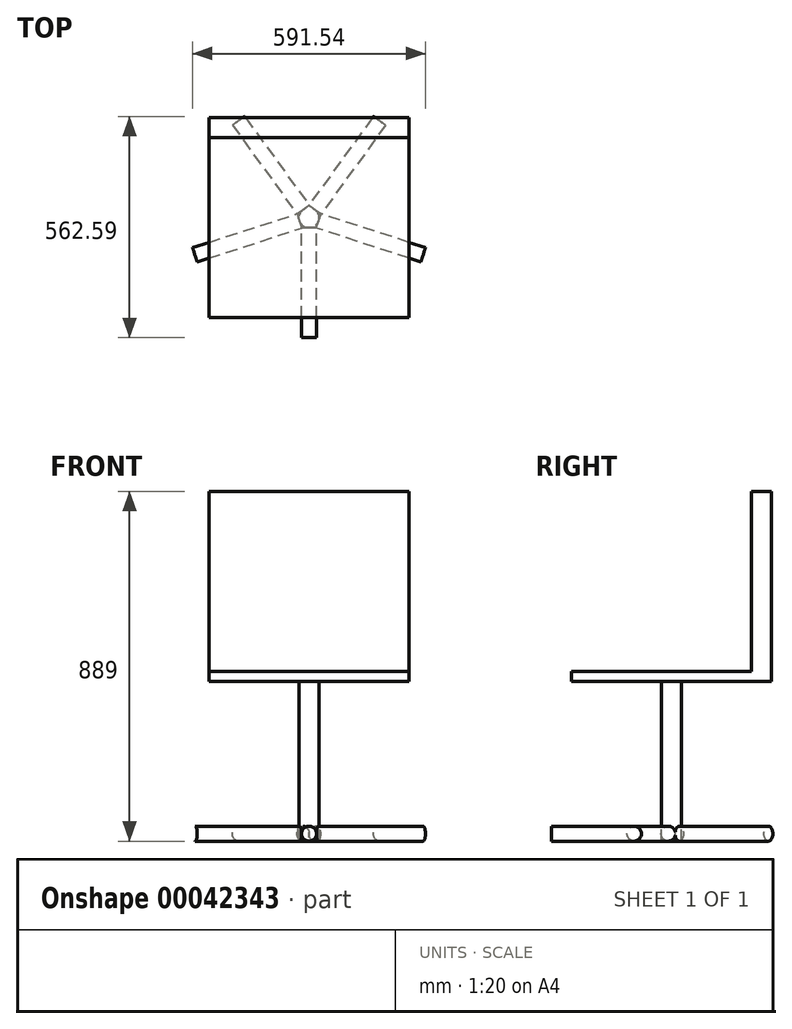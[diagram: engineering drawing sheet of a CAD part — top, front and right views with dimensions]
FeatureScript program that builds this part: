
annotation { "Feature Type Name" : "Feature", "Feature Type Description" : "" }
export const myFeature = defineFeature(function(context is Context, id is Id, definition is map)
    precondition{}
    {
        {
            var Q0;
            Q0=qCreatedBy(makeId("Top.planeOp"),FACE);
            var sketch = newSketch(context, id + "F0", { "sketchPlane" : qUnion([Q0])});
            skLineSegment(sketch, "E0.rect.bottom", {"start": v(254, 254) * mm, "end": v(-254, 254) * mm});
            skLineSegment(sketch, "E0.rect.top", {"start": v(254, -254) * mm, "end": v(-254, -254) * mm});
            skLineSegment(sketch, "E0.rect.left", {"start": v(254, 254) * mm, "end": v(254, -254) * mm});
            skLineSegment(sketch, "E0.rect.right", {"start": v(-254, 254) * mm, "end": v(-254, -254) * mm});
            skPoint(sketch, "E0.rect.middle", {"position": v(0, 0) * mm});
            skSolve(sketch);
        }
        {
            var Q0;
            Q0=qSketchRegion(id+"F0",true);
            extrude(context, id + "F1", {"entities" : qUnion([Q0]), "oppositeDirection" : true, "depth" : 25.4 * mm});
        }
        {
            var Q0;
            Q0=makeQuery(id+"F1.opExtrude","CAP_FACE",FACE,{"disambiguationData":[OSD([sQuery(id+"F0.wireOp",EDGE,"E0.rect.bottom"),sQuery(id+"F0.wireOp",EDGE,"E0.rect.top"),sQuery(id+"F0.wireOp",EDGE,"E0.rect.left"),sQuery(id+"F0.wireOp",EDGE,"E0.rect.right")])],"isStart":true});
            var sketch = newSketch(context, id + "F2", { "sketchPlane" : qUnion([Q0])});
            skLineSegment(sketch, "E1.bottom", {"start": v(-254, 254) * mm, "end": v(254, 254) * mm});
            skLineSegment(sketch, "E1.top", {"start": v(-254, 203.2) * mm, "end": v(254, 203.2) * mm});
            skLineSegment(sketch, "E1.left", {"start": v(-254, 254) * mm, "end": v(-254, 203.2) * mm});
            skLineSegment(sketch, "E1.right", {"start": v(254, 254) * mm, "end": v(254, 203.2) * mm});
            skSolve(sketch);
        }
        {
            var Q0;
            Q0=qSketchRegion(id+"F2",true);
            extrude(context, id + "F3", {"entities" : qUnion([Q0]), "operationType" : NewBodyOperationType.ADD, "depth" : 457.2 * mm});
        }
        {
            var Q0;
            Q0=makeQuery(id+"F1.opExtrude","CAP_FACE",FACE,{"disambiguationData":[OSD([sQuery(id+"F0.wireOp",EDGE,"E0.rect.bottom"),sQuery(id+"F0.wireOp",EDGE,"E0.rect.top"),sQuery(id+"F0.wireOp",EDGE,"E0.rect.left"),sQuery(id+"F0.wireOp",EDGE,"E0.rect.right")])],"isStart":false});
            var sketch = newSketch(context, id + "F4", { "sketchPlane" : qUnion([Q0])});
            skCircle(sketch, "E2", {"center": v(0, 0) * mm, "radius": 25.4 * mm});
            skSolve(sketch);
        }
        {
            var Q0;
            Q0=makeQuery(id+"F4.imprint","IMPRINT",FACE,{"disambiguationData":[TD([[makeQuery(id+"F4.imprint","IMPRINT",EDGE,{"derivedFrom":sQuery(id+"F4.wireOp",EDGE,"E2")}),1.0]])]});
            extrude(context, id + "F5", {"entities" : qUnion([Q0]), "operationType" : NewBodyOperationType.ADD, "depth" : 406.4 * mm});
        }
        {
            var Q0;
            Q0=qCreatedBy(makeId("Front.planeOp"),FACE);
            cPlane(context, id + "F6", {"entities" : qUnion([Q0]), "cplaneType" : CPlaneType.OFFSET, "offset" : 25.4 * mm, "width" : 152.4 * mm, "height" : 152.4 * mm});
        }
        {
            var Q0;
            Q0=qCreatedBy(id+"F6.planeOp",FACE);
            var sketch = newSketch(context, id + "F7", { "sketchPlane" : qUnion([Q0])});
            skCircle(sketch, "E3", {"center": v(0, -412.75) * mm, "radius": 19.05 * mm});
            skSolve(sketch);
        }
        {
            var Q0;
            Q0=makeQuery(id+"F7.imprint","IMPRINT",FACE,{"disambiguationData":[TD([[makeQuery(id+"F7.imprint","IMPRINT",EDGE,{"derivedFrom":sQuery(id+"F7.wireOp",EDGE,"E3")}),1.0]])]});
            extrude(context, id + "F8", {"entities" : qUnion([Q0]), "depth" : 279.4 * mm});
        }
        {
            var Q0;
            Q0=qCreatedBy(makeId("Right.planeOp"),FACE);
            var sketch = newSketch(context, id + "F9", { "sketchPlane" : qUnion([Q0])});
            skLineSegment(sketch, "E4", {"start": v(0, 0) * mm, "end": v(0, -315.06) * mm, "construction": true});
            skSolve(sketch);
        }
        {
            var Q0;
            Q0=makeQuery(id+"F8.opExtrude","SWEPT_BODY",BODY,{"disambiguationData":[OSD([sQuery(id+"F7.wireOp",EDGE,"E3")])]});
            var Q1;
            Q1=sQuery(id+"F9.wireOp",EDGE,"E4");
            circularPattern(context, id + "F10", {"entities" : qUnion([Q0]), "axis" : qUnion([Q1]), "angle" : 360 * degree, "instanceCount" : round(5), "equalSpace" : true});
        }
    });
